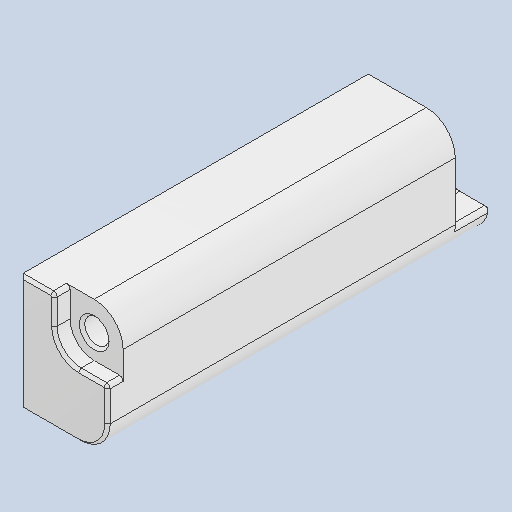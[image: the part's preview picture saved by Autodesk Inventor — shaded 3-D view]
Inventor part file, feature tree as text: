
AUTODESK INVENTOR PART (.ipt)
format: ipt  version: 2023.3 (Build 273359000, 359)  size: 196,608 bytes
history: native  units: mm
features: fillet x5, sketch x5, extrude x4, chamfer x2, hole x1
ambient origin geometry x8: Origin, YZ Plane, XZ Plane, XY Plane, X Axis, Y Axis, Z Axis, Center Point
bodies: Solid1 (feature_tree)
feature tree (17):
  extrude  "Extrusion1"  Depth=25.4mm
  extrude  "Extrusion2"  Depth=11.621mm
  extrude  "Extrusion3"  Depth=3.429mm TaperAngle=0.0deg
  hole  "Hole1"  [1 undecoded]
  fillet  "Fillet1"  Radius=7.938mm
  fillet  "Fillet2"  Radius=6.35mm
  fillet  "Fillet3"  Radius=6.35mm
  fillet  "Fillet4"  Radius=6.35mm
  chamfer  "Chamfer1"  Distance=0.794mm
  extrude  "Extrusion4"  Depth=5.271mm
  fillet  "Fillet5"  Radius=13.208mm
  chamfer  "Chamfer2"  Distance=0.6mm Angle=45.0deg
  sketch  "Sketch1"  dims[d0=25.4mm d1=25.4mm]
  sketch  "Sketch2"  dims[d2=84.138mm d3=0.0mm d4=11.621mm]
  sketch  "Sketch3"  dims[d5=11.621mm d6=3.429mm d7=0.0mm]
  sketch  "Sketch4"  dims[d8=19.558mm d9=19.558mm d10=7.938mm d11=0.0mm d12=6.35mm d13=6.35mm]
  sketch  "Sketch5"  dims[d14=5.334mm d15=6.0mm d16=9.779mm d17=2.0mm d18=14.3117mm d19=8.0mm d20=20.594885mm d21=6.35mm d22=0.794mm d23=5.271mm d24=13.208mm d25=0.6mm d26=2.0mm d27=45.0deg d28=25.4mm d29=6.35mm d30=84.138mm d31=0.0mm d32=0.794mm d33=0.6mm d34=2.0mm d35=45.0deg]
note: 1 required parameter value undecoded (feature->parameter linkage not recoverable at this tier; creation-order binding heuristic only, values carry confidence <= 0.55)
